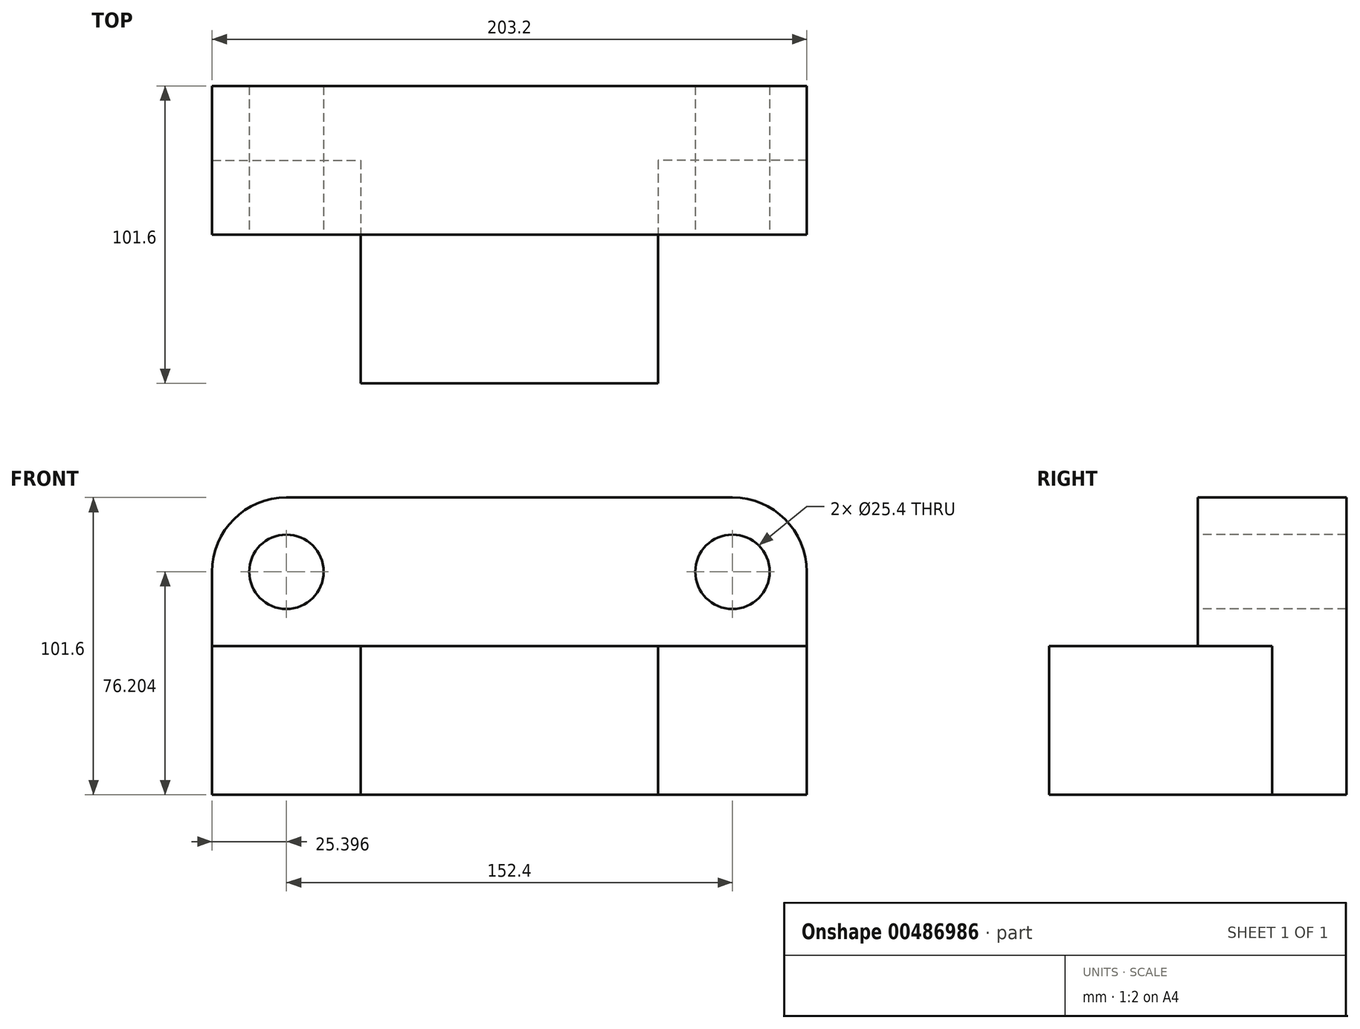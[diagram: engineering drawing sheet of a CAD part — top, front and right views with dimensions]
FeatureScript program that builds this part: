
annotation { "Feature Type Name" : "Feature", "Feature Type Description" : "" }
export const myFeature = defineFeature(function(context is Context, id is Id, definition is map)
    precondition{}
    {
        {
            var Q0;
            Q0=qCreatedBy(makeId("Front.planeOp"),FACE);
            var sketch = newSketch(context, id + "F0", { "sketchPlane" : qUnion([Q0])});
            skLineSegment(sketch, "E0.bottom", {"start": v(-105.23, 41.31) * mm, "end": v(97.97, 41.31) * mm});
            skLineSegment(sketch, "E0.top", {"start": v(-105.23, -60.29) * mm, "end": v(97.97, -60.29) * mm});
            skLineSegment(sketch, "E0.left", {"start": v(-105.23, 41.31) * mm, "end": v(-105.23, -60.29) * mm});
            skLineSegment(sketch, "E0.right", {"start": v(97.97, 41.31) * mm, "end": v(97.97, -60.29) * mm});
            skSolve(sketch);
        }
        {
            var Q0;
            Q0=makeQuery(id+"F0.imprint","IMPRINT",FACE,{"disambiguationData":[TD([[makeQuery(id+"F0.imprint","IMPRINT",EDGE,{"derivedFrom":sQuery(id+"F0.wireOp",EDGE,"E0.bottom")}),-1.0]])]});
            extrude(context, id + "F1", {"entities" : qUnion([Q0]), "depth" : 101.6 * mm});
        }
        {
            var Q0;
            Q0=makeQuery(id+"F1.opExtrude","CAP_FACE",FACE,{"disambiguationData":[OSD([sQuery(id+"F0.wireOp",EDGE,"E0.bottom"),sQuery(id+"F0.wireOp",EDGE,"E0.top"),sQuery(id+"F0.wireOp",EDGE,"E0.left"),sQuery(id+"F0.wireOp",EDGE,"E0.right")])],"isStart":false});
            var sketch = newSketch(context, id + "F2", { "sketchPlane" : qUnion([Q0])});
            skLineSegment(sketch, "E1.bottom", {"start": v(97.97, -60.29) * mm, "end": v(47.17, -60.29) * mm});
            skLineSegment(sketch, "E1.top", {"start": v(97.97, -9.49) * mm, "end": v(47.17, -9.49) * mm});
            skLineSegment(sketch, "E1.left", {"start": v(97.97, -60.29) * mm, "end": v(97.97, -9.49) * mm});
            skLineSegment(sketch, "E1.right", {"start": v(47.17, -60.29) * mm, "end": v(47.17, -9.49) * mm});
            skSolve(sketch);
        }
        {
            var Q0;
            Q0=makeQuery(id+"F2.imprint","IMPRINT",FACE,{"disambiguationData":[TD([[makeQuery(id+"F2.imprint","IMPRINT",EDGE,{"derivedFrom":sQuery(id+"F2.wireOp",EDGE,"E1.bottom")}),1.0]])]});
            extrude(context, id + "F3", {"entities" : qUnion([Q0]), "operationType" : NewBodyOperationType.REMOVE, "oppositeDirection" : true, "depth" : 76.2 * mm});
        }
        {
            var Q0;
            Q0=makeQuery(id+"F1.opExtrude","CAP_FACE",FACE,{"disambiguationData":[OSD([sQuery(id+"F0.wireOp",EDGE,"E0.bottom"),sQuery(id+"F0.wireOp",EDGE,"E0.top"),sQuery(id+"F0.wireOp",EDGE,"E0.left"),sQuery(id+"F0.wireOp",EDGE,"E0.right")])],"isStart":false});
            var sketch = newSketch(context, id + "F4", { "sketchPlane" : qUnion([Q0])});
            skLineSegment(sketch, "E2.bottom", {"start": v(-105.23, -60.29) * mm, "end": v(-54.43, -60.29) * mm});
            skLineSegment(sketch, "E2.top", {"start": v(-105.23, -9.49) * mm, "end": v(-54.43, -9.49) * mm});
            skLineSegment(sketch, "E2.left", {"start": v(-105.23, -60.29) * mm, "end": v(-105.23, -9.49) * mm});
            skLineSegment(sketch, "E2.right", {"start": v(-54.43, -60.29) * mm, "end": v(-54.43, -9.49) * mm});
            skSolve(sketch);
        }
        {
            var Q0;
            Q0=makeQuery(id+"F4.imprint","IMPRINT",FACE,{"disambiguationData":[TD([[makeQuery(id+"F4.imprint","IMPRINT",EDGE,{"derivedFrom":sQuery(id+"F4.wireOp",EDGE,"E2.bottom")}),1.0]])]});
            extrude(context, id + "F5", {"entities" : qUnion([Q0]), "operationType" : NewBodyOperationType.REMOVE, "oppositeDirection" : true, "depth" : 76.2 * mm});
        }
        {
            var Q0;
            Q0=makeQuery(id+"F1.opExtrude","CAP_FACE",FACE,{"disambiguationData":[OSD([sQuery(id+"F0.wireOp",EDGE,"E0.bottom"),sQuery(id+"F0.wireOp",EDGE,"E0.top"),sQuery(id+"F0.wireOp",EDGE,"E0.left"),sQuery(id+"F0.wireOp",EDGE,"E0.right")])],"isStart":false});
            var sketch = newSketch(context, id + "F6", { "sketchPlane" : qUnion([Q0])});
            skLineSegment(sketch, "E3", {"start": v(97.97, 41.31) * mm, "end": v(72.57, 41.31) * mm});
            skLineSegment(sketch, "E4", {"start": v(97.97, 41.31) * mm, "end": v(97.97, 15.91) * mm});
            skArc(sketch, "E5", {"start": v(97.97, 15.91) * mm, "mid": v(90.53, 33.87) * mm, "end": v(72.57, 41.31) * mm});
            skSolve(sketch);
        }
        {
            var Q0;
            Q0=makeQuery(id+"F6.imprint","IMPRINT",FACE,{"disambiguationData":[TD([[makeQuery(id+"F6.imprint","IMPRINT",EDGE,{"derivedFrom":sQuery(id+"F6.wireOp",EDGE,"E3")}),-1.0]])]});
            extrude(context, id + "F7", {"entities" : qUnion([Q0]), "operationType" : NewBodyOperationType.REMOVE, "oppositeDirection" : true, "depth" : 101.6 * mm});
        }
        {
            var Q0;
            Q0=makeQuery(id+"F1.opExtrude","CAP_FACE",FACE,{"disambiguationData":[OSD([sQuery(id+"F0.wireOp",EDGE,"E0.bottom"),sQuery(id+"F0.wireOp",EDGE,"E0.top"),sQuery(id+"F0.wireOp",EDGE,"E0.left"),sQuery(id+"F0.wireOp",EDGE,"E0.right")])],"isStart":false});
            var sketch = newSketch(context, id + "F8", { "sketchPlane" : qUnion([Q0])});
            skLineSegment(sketch, "E6", {"start": v(-105.23, 41.31) * mm, "end": v(-105.23, 15.91) * mm});
            skLineSegment(sketch, "E7", {"start": v(-105.23, 41.31) * mm, "end": v(-79.83, 41.31) * mm});
            skArc(sketch, "E8", {"start": v(-79.83, 41.31) * mm, "mid": v(-97.8, 33.87) * mm, "end": v(-105.23, 15.91) * mm});
            skSolve(sketch);
        }
        {
            var Q0;
            Q0=makeQuery(id+"F8.imprint","IMPRINT",FACE,{"disambiguationData":[TD([[makeQuery(id+"F8.imprint","IMPRINT",EDGE,{"derivedFrom":sQuery(id+"F8.wireOp",EDGE,"E6")}),1.0]])]});
            extrude(context, id + "F9", {"entities" : qUnion([Q0]), "operationType" : NewBodyOperationType.REMOVE, "oppositeDirection" : true, "depth" : 101.6 * mm});
        }
        {
            var Q0;
            Q0=makeQuery(id+"F1.opExtrude","CAP_FACE",FACE,{"disambiguationData":[OSD([sQuery(id+"F0.wireOp",EDGE,"E0.bottom"),sQuery(id+"F0.wireOp",EDGE,"E0.top"),sQuery(id+"F0.wireOp",EDGE,"E0.left"),sQuery(id+"F0.wireOp",EDGE,"E0.right")])],"isStart":false});
            var sketch = newSketch(context, id + "F10", { "sketchPlane" : qUnion([Q0])});
            skLineSegment(sketch, "E9", {"start": v(72.57, 41.31) * mm, "end": v(72.57, 15.91) * mm});
            skCircle(sketch, "E10", {"center": v(72.57, 15.91) * mm, "radius": 12.7 * mm});
            skSolve(sketch);
        }
        {
            var Q0;
            Q0=makeQuery(id+"F10.imprint","IMPRINT",FACE,{"disambiguationData":[TD([[makeQuery(id+"F10.imprint","IMPRINT",EDGE,{"derivedFrom":sQuery(id+"F10.wireOp",EDGE,"E10")}),1.0]])]});
            extrude(context, id + "F11", {"entities" : qUnion([Q0]), "operationType" : NewBodyOperationType.REMOVE, "oppositeDirection" : true, "depth" : 101.6 * mm});
        }
        {
            var Q0;
            Q0=makeQuery(id+"F1.opExtrude","CAP_FACE",FACE,{"disambiguationData":[OSD([sQuery(id+"F0.wireOp",EDGE,"E0.bottom"),sQuery(id+"F0.wireOp",EDGE,"E0.top"),sQuery(id+"F0.wireOp",EDGE,"E0.left"),sQuery(id+"F0.wireOp",EDGE,"E0.right")])],"isStart":false});
            var sketch = newSketch(context, id + "F12", { "sketchPlane" : qUnion([Q0])});
            skLineSegment(sketch, "E11", {"start": v(-79.83, 41.31) * mm, "end": v(-79.83, 15.91) * mm});
            skCircle(sketch, "E12", {"center": v(-79.83, 15.91) * mm, "radius": 12.7 * mm});
            skSolve(sketch);
        }
        {
            var Q0;
            Q0=makeQuery(id+"F12.imprint","IMPRINT",FACE,{"disambiguationData":[TD([[makeQuery(id+"F12.imprint","IMPRINT",EDGE,{"derivedFrom":sQuery(id+"F12.wireOp",EDGE,"E12")}),1.0]])]});
            extrude(context, id + "F13", {"entities" : qUnion([Q0]), "operationType" : NewBodyOperationType.REMOVE, "oppositeDirection" : true, "depth" : 101.6 * mm});
        }
        {
            var Q0;
            Q0=makeQuery(id+"F1.opExtrude","CAP_FACE",FACE,{"disambiguationData":[OSD([sQuery(id+"F0.wireOp",EDGE,"E0.bottom"),sQuery(id+"F0.wireOp",EDGE,"E0.top"),sQuery(id+"F0.wireOp",EDGE,"E0.left"),sQuery(id+"F0.wireOp",EDGE,"E0.right")])],"isStart":false});
            var sketch = newSketch(context, id + "F14", { "sketchPlane" : qUnion([Q0])});
            skLineSegment(sketch, "E13.bottom", {"start": v(-105.23, -9.49) * mm, "end": v(97.97, -9.49) * mm});
            skLineSegment(sketch, "E13.top", {"start": v(-105.23, 41.31) * mm, "end": v(97.97, 41.31) * mm});
            skLineSegment(sketch, "E13.left", {"start": v(-105.23, -9.49) * mm, "end": v(-105.23, 41.31) * mm});
            skLineSegment(sketch, "E13.right", {"start": v(97.97, -9.49) * mm, "end": v(97.97, 41.31) * mm});
            skSolve(sketch);
        }
        {
            var Q0;
            Q0 = qSketchRegion(id + "F14", true);
            extrude(context, id + "F15", {"entities" : qUnion([Q0]), "operationType" : NewBodyOperationType.REMOVE, "oppositeDirection" : true, "depth" : 50.8 * mm});
        }
    });
